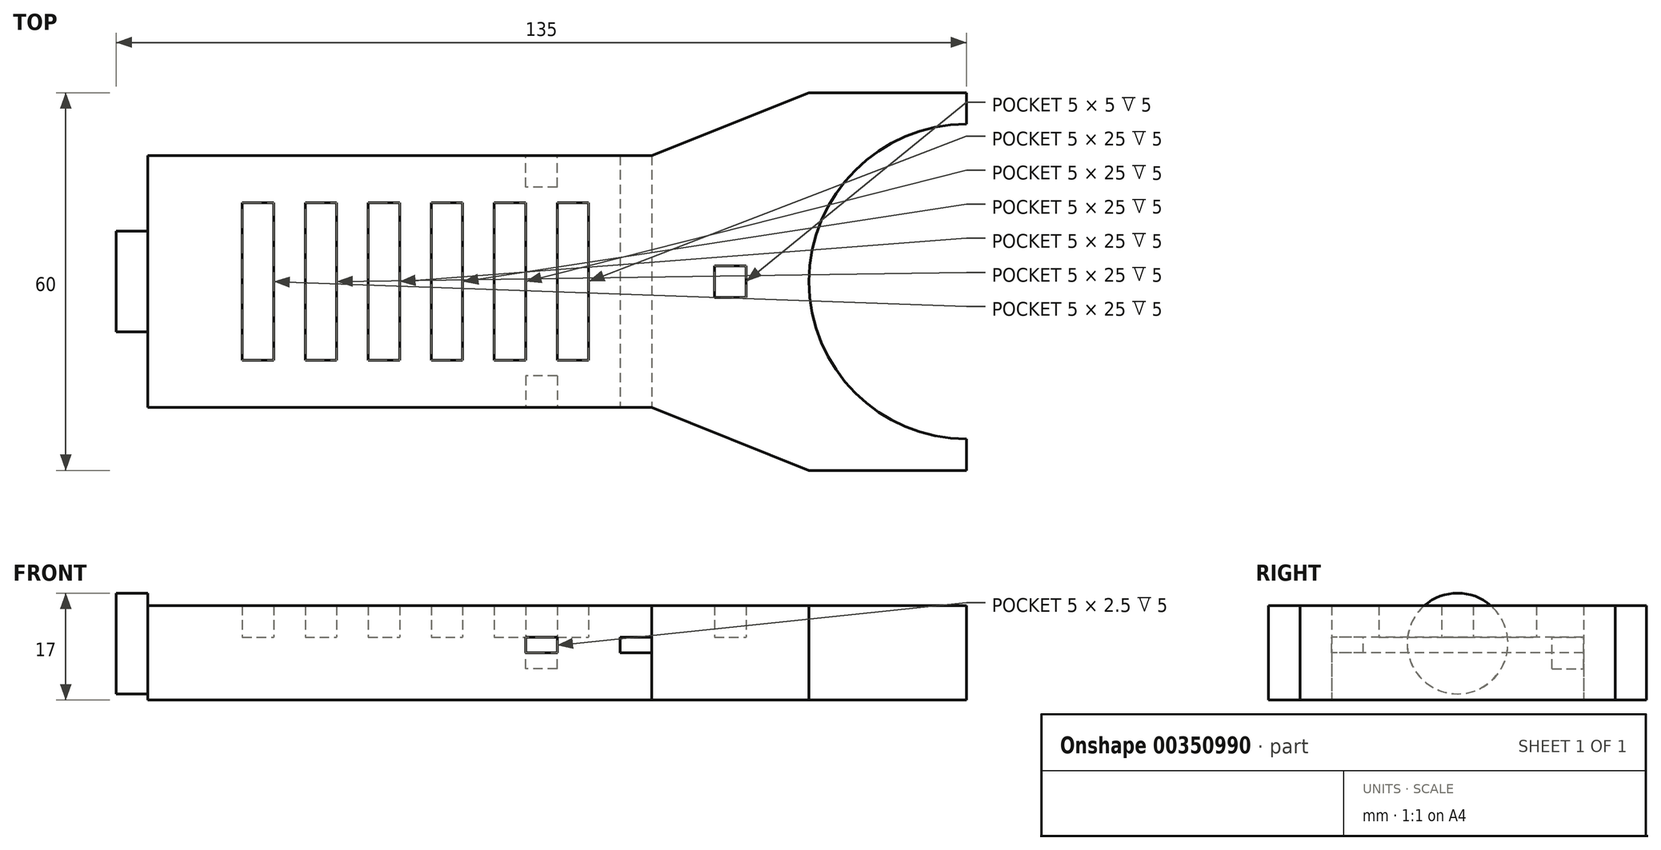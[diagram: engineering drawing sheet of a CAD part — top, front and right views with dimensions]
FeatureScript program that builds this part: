
annotation { "Feature Type Name" : "Feature", "Feature Type Description" : "" }
export const myFeature = defineFeature(function(context is Context, id is Id, definition is map)
    precondition{}
    {
        {
            var Q0;
            Q0=qCreatedBy(makeId("Top.planeOp"),FACE);
            var sketch = newSketch(context, id + "F0", { "sketchPlane" : qUnion([Q0])});
            skArc(sketch, "E0", {"start": v(46.11, 25) * mm, "mid": v(21.11, 0) * mm, "end": v(46.11, -25) * mm});
            skLineSegment(sketch, "E1", {"start": v(46.11, 25) * mm, "end": v(46.11, 30) * mm});
            skLineSegment(sketch, "E2", {"start": v(46.11, 30) * mm, "end": v(21.11, 30) * mm});
            skLineSegment(sketch, "E3", {"start": v(46.11, -25) * mm, "end": v(46.11, -30) * mm});
            skLineSegment(sketch, "E4", {"start": v(46.11, -30) * mm, "end": v(21.11, -30) * mm});
            skPoint(sketch, "E5", {"position": v(-3.89, 20) * mm});
            skPoint(sketch, "E6", {"position": v(-3.89, -20) * mm});
            skLineSegment(sketch, "E7", {"start": v(21.11, -30) * mm, "end": v(-3.89, -20) * mm});
            skLineSegment(sketch, "E8", {"start": v(21.11, 30) * mm, "end": v(-3.89, 20) * mm});
            skLineSegment(sketch, "E9", {"start": v(-3.89, 20) * mm, "end": v(-71.39, 20) * mm});
            skLineSegment(sketch, "E10", {"start": v(-71.39, -20) * mm, "end": v(-3.89, -20) * mm});
            skLineSegment(sketch, "E11", {"start": v(21.11, 0) * mm, "end": v(11.11, 0) * mm, "construction": true});
            skLineSegment(sketch, "E12", {"start": v(11.11, 0) * mm, "end": v(11.11, 2.5) * mm});
            skLineSegment(sketch, "E13", {"start": v(11.11, 2.5) * mm, "end": v(6.11, 2.5) * mm});
            skLineSegment(sketch, "E14", {"start": v(6.11, 2.5) * mm, "end": v(6.11, -2.5) * mm});
            skLineSegment(sketch, "E15", {"start": v(6.11, -2.5) * mm, "end": v(11.11, -2.5) * mm});
            skLineSegment(sketch, "E16", {"start": v(11.11, -2.5) * mm, "end": v(11.11, 0) * mm});
            skLineSegment(sketch, "E17", {"start": v(6.11, 0) * mm, "end": v(-13.89, 0) * mm, "construction": true});
            skLineSegment(sketch, "E18", {"start": v(-13.89, 0) * mm, "end": v(-13.89, 12.5) * mm});
            skLineSegment(sketch, "E19", {"start": v(-13.89, 12.5) * mm, "end": v(-18.89, 12.5) * mm});
            skLineSegment(sketch, "E20", {"start": v(-18.89, 12.5) * mm, "end": v(-18.89, -12.5) * mm});
            skLineSegment(sketch, "E21", {"start": v(-18.89, -12.5) * mm, "end": v(-13.89, -12.5) * mm});
            skLineSegment(sketch, "E22", {"start": v(-13.89, -12.5) * mm, "end": v(-13.89, 0) * mm});
            skLineSegment(sketch, "E23", {"start": v(-18.89, 0) * mm, "end": v(-23.89, 0) * mm, "construction": true});
            skLineSegment(sketch, "E24", {"start": v(-23.89, 0) * mm, "end": v(-23.89, 12.5) * mm});
            skLineSegment(sketch, "E25", {"start": v(-23.89, 12.5) * mm, "end": v(-28.89, 12.5) * mm});
            skLineSegment(sketch, "E26", {"start": v(-28.89, 12.5) * mm, "end": v(-28.89, -12.5) * mm});
            skLineSegment(sketch, "E27", {"start": v(-28.89, -12.5) * mm, "end": v(-23.89, -12.5) * mm});
            skLineSegment(sketch, "E28", {"start": v(-23.89, -12.5) * mm, "end": v(-23.89, 0) * mm});
            skLineSegment(sketch, "E29", {"start": v(-28.89, 0) * mm, "end": v(-33.89, 0) * mm, "construction": true});
            skPoint(sketch, "E29.endSnap0", {"position": v(-28.89, 0) * mm});
            skLineSegment(sketch, "E30", {"start": v(-33.89, 0) * mm, "end": v(-33.89, 12.5) * mm});
            skLineSegment(sketch, "E31", {"start": v(-33.89, 12.5) * mm, "end": v(-38.89, 12.5) * mm});
            skLineSegment(sketch, "E32", {"start": v(-38.89, 12.5) * mm, "end": v(-38.89, -12.5) * mm});
            skLineSegment(sketch, "E33", {"start": v(-38.89, -12.5) * mm, "end": v(-33.89, -12.5) * mm});
            skLineSegment(sketch, "E34", {"start": v(-33.89, -12.5) * mm, "end": v(-33.89, 0) * mm});
            skLineSegment(sketch, "E35", {"start": v(-38.89, 0) * mm, "end": v(-43.89, 0) * mm, "construction": true});
            skLineSegment(sketch, "E36", {"start": v(-43.89, 0) * mm, "end": v(-43.89, 12.5) * mm});
            skLineSegment(sketch, "E37", {"start": v(-43.89, 12.5) * mm, "end": v(-48.89, 12.5) * mm});
            skLineSegment(sketch, "E38", {"start": v(-48.89, 12.5) * mm, "end": v(-48.89, -12.5) * mm});
            skLineSegment(sketch, "E39", {"start": v(-48.89, -12.5) * mm, "end": v(-43.89, -12.5) * mm});
            skLineSegment(sketch, "E40", {"start": v(-43.89, -12.5) * mm, "end": v(-43.89, 0) * mm});
            skLineSegment(sketch, "E41", {"start": v(-48.89, 0) * mm, "end": v(-53.89, 0) * mm, "construction": true});
            skLineSegment(sketch, "E42", {"start": v(-53.89, 0) * mm, "end": v(-53.89, 12.5) * mm});
            skLineSegment(sketch, "E43", {"start": v(-53.89, 12.5) * mm, "end": v(-58.89, 12.5) * mm});
            skLineSegment(sketch, "E44", {"start": v(-58.89, 12.5) * mm, "end": v(-58.89, -12.5) * mm});
            skLineSegment(sketch, "E45", {"start": v(-58.89, -12.5) * mm, "end": v(-53.89, -12.5) * mm});
            skLineSegment(sketch, "E46", {"start": v(-53.89, -12.5) * mm, "end": v(-53.89, 0) * mm});
            skLineSegment(sketch, "E47", {"start": v(-58.89, 0) * mm, "end": v(-63.89, 0) * mm, "construction": true});
            skLineSegment(sketch, "E48", {"start": v(-63.89, 0) * mm, "end": v(-63.89, 12.5) * mm});
            skLineSegment(sketch, "E49", {"start": v(-63.89, 12.5) * mm, "end": v(-68.89, 12.5) * mm});
            skLineSegment(sketch, "E50", {"start": v(-68.89, 12.5) * mm, "end": v(-68.89, -12.5) * mm});
            skLineSegment(sketch, "E51", {"start": v(-68.89, -12.5) * mm, "end": v(-63.89, -12.5) * mm});
            skLineSegment(sketch, "E52", {"start": v(-63.89, -12.5) * mm, "end": v(-63.89, 0) * mm});
            skLineSegment(sketch, "E53", {"start": v(-71.39, -20) * mm, "end": v(-71.39, 20) * mm});
            skSolve(sketch);
        }
        {
            var Q0;
            Q0=makeQuery(id+"F0.imprint","IMPRINT",FACE,{"disambiguationData":[TD([[makeQuery(id+"F0.imprint","IMPRINT",EDGE,{"derivedFrom":sQuery(id+"F0.wireOp",EDGE,"E0")}),-1.0]])]});
            extrude(context, id + "F1", {"entities" : qUnion([Q0]), "depth" : 15 * mm});
        }
        {
            var Q0;
            Q0=makeQuery(id+"F1.opExtrude","SWEPT_FACE",FACE,{"disambiguationData":[OSD([sQuery(id+"F0.wireOp",EDGE,"E53")])]});
            extrude(context, id + "F2", {"entities" : qUnion([Q0]), "operationType" : NewBodyOperationType.ADD, "depth" : 12.5 * mm});
        }
        {
            var Q0;
            Q0=makeQuery(id+"F2.opExtrude","CAP_FACE",FACE,{"disambiguationData":[OSD([sQuery(id+"F0.wireOp",EDGE,"E53")])],"isStart":false});
            var sketch = newSketch(context, id + "F3", { "sketchPlane" : qUnion([Q0])});
            skLineSegment(sketch, "E54", {"start": v(0, 0) * mm, "end": v(0, 9) * mm, "construction": true});
            skCircle(sketch, "E55", {"center": v(0, 9) * mm, "radius": 8 * mm});
            skSolve(sketch);
        }
        {
            var Q0;
            {var subQ0=sQuery(id+"F3.wireOp",EDGE,"E55");var subQ1=sQuery(id+"F0.wireOp",EDGE,"E53");var subQ2=makeQuery(id+"F2.opExtrude","CAP_EDGE",EDGE,{"disambiguationData":[OSD([subQ1]),TDD([makeQuery(id+"F1.opExtrude","CAP_EDGE",EDGE,{"disambiguationData":[OSD([subQ1])],"isStart":false})])],"isStart":false});var subQ3=makeQuery(id+"F3.imprint","INTERSECT",VERTEX,{"disambiguationData":[OD(0.0)],"derivedFrom":[subQ2,subQ0]});Q0=makeQuery(id+"F3.imprint","IMPRINT",FACE,{"disambiguationData":[TD([[makeQuery(id+"F3.imprint","IMPRINT",EDGE,{"disambiguationData":[TD([[subQ3,1.0]])],"derivedFrom":subQ0}),1.0]])]});}
            var Q1;
            {var subQ0=sQuery(id+"F3.wireOp",EDGE,"E55");var subQ1=sQuery(id+"F0.wireOp",EDGE,"E53");var subQ2=makeQuery(id+"F2.opExtrude","CAP_EDGE",EDGE,{"disambiguationData":[OSD([subQ1]),TDD([makeQuery(id+"F1.opExtrude","CAP_EDGE",EDGE,{"disambiguationData":[OSD([subQ1])],"isStart":false})])],"isStart":false});var subQ3=makeQuery(id+"F3.imprint","INTERSECT",VERTEX,{"disambiguationData":[OD(0.0)],"derivedFrom":[subQ2,subQ0]});Q1=makeQuery(id+"F3.imprint","IMPRINT",FACE,{"disambiguationData":[TD([[makeQuery(id+"F3.imprint","IMPRINT",EDGE,{"disambiguationData":[TD([[subQ3,-1.0]])],"derivedFrom":subQ0}),1.0]])]});}
            extrude(context, id + "F4", {"entities" : qUnion([Q0, Q1]), "operationType" : NewBodyOperationType.ADD, "depth" : 5 * mm});
        }
        {
            var Q0;
            {var subQ0=sQuery(id+"F0.wireOp",EDGE,"E10");Q0=makeQuery(id+"F2.boolean.opBoolean","MERGE",FACE,{"derivedFrom":[makeQuery(id+"F1.opExtrude","SWEPT_FACE",FACE,{"disambiguationData":[OSD([subQ0])]}),makeQuery(id+"F2.opExtrude","SWEPT_FACE",FACE,{"disambiguationData":[OSD([subQ0,sQuery(id+"F0.wireOp",EDGE,"E53")])]})]});}
            var sketch = newSketch(context, id + "F5", { "sketchPlane" : qUnion([Q0])});
            skLineSegment(sketch, "E56.bottom", {"start": v(-3.89, 7.5) * mm, "end": v(-8.89, 7.5) * mm});
            skLineSegment(sketch, "E56.top", {"start": v(-3.89, 10) * mm, "end": v(-8.89, 10) * mm});
            skLineSegment(sketch, "E56.left", {"start": v(-3.89, 7.5) * mm, "end": v(-3.89, 10) * mm});
            skLineSegment(sketch, "E56.right", {"start": v(-8.89, 7.5) * mm, "end": v(-8.89, 10) * mm});
            skLineSegment(sketch, "E57.bottom", {"start": v(-8.89, 7.5) * mm, "end": v(-3.89, 7.5) * mm});
            skLineSegment(sketch, "E57.top", {"start": v(-8.89, 5) * mm, "end": v(-3.89, 5) * mm});
            skLineSegment(sketch, "E57.left", {"start": v(-8.89, 7.5) * mm, "end": v(-8.89, 5) * mm});
            skLineSegment(sketch, "E57.right", {"start": v(-3.89, 7.5) * mm, "end": v(-3.89, 5) * mm});
            skSolve(sketch);
        }
        {
            var Q0;
            Q0=makeQuery(id+"F5.imprint","IMPRINT",FACE,{"disambiguationData":[TD([[makeQuery(id+"F5.imprint","IMPRINT",EDGE,{"derivedFrom":sQuery(id+"F5.wireOp",EDGE,"E57.bottom")}),-1.0]])]});
            var Q1;
            Q1=makeQuery(id+"F5.imprint","IMPRINT",FACE,{"disambiguationData":[TD([[makeQuery(id+"F5.imprint","IMPRINT",EDGE,{"derivedFrom":sQuery(id+"F5.wireOp",EDGE,"E56.top")}),1.0]])]});
            extrude(context, id + "F6", {"entities" : qUnion([Q0, Q1]), "operationType" : NewBodyOperationType.REMOVE, "oppositeDirection" : true, "depth" : 50 * mm});
        }
        {
            var Q0;
            {var subQ0=sQuery(id+"F0.wireOp",EDGE,"E10");Q0=makeQuery(id+"F2.boolean.opBoolean","MERGE",FACE,{"derivedFrom":[makeQuery(id+"F1.opExtrude","SWEPT_FACE",FACE,{"disambiguationData":[OSD([subQ0])]}),makeQuery(id+"F2.opExtrude","SWEPT_FACE",FACE,{"disambiguationData":[OSD([subQ0,sQuery(id+"F0.wireOp",EDGE,"E53")])]})]});}
            var sketch = newSketch(context, id + "F7", { "sketchPlane" : qUnion([Q0])});
            skLineSegment(sketch, "E58", {"start": v(-8.89, 7.5) * mm, "end": v(-18.89, 7.5) * mm, "construction": true});
            skLineSegment(sketch, "E59.bottom", {"start": v(-18.89, 7.5) * mm, "end": v(-23.89, 7.5) * mm});
            skLineSegment(sketch, "E59.top", {"start": v(-18.89, 10) * mm, "end": v(-23.89, 10) * mm});
            skLineSegment(sketch, "E59.left", {"start": v(-18.89, 7.5) * mm, "end": v(-18.89, 10) * mm});
            skLineSegment(sketch, "E59.right", {"start": v(-23.89, 7.5) * mm, "end": v(-23.89, 10) * mm});
            skLineSegment(sketch, "E60.bottom", {"start": v(-23.89, 7.5) * mm, "end": v(-18.89, 7.5) * mm});
            skLineSegment(sketch, "E60.top", {"start": v(-23.89, 5) * mm, "end": v(-18.89, 5) * mm});
            skLineSegment(sketch, "E60.left", {"start": v(-23.89, 7.5) * mm, "end": v(-23.89, 5) * mm});
            skLineSegment(sketch, "E60.right", {"start": v(-18.89, 7.5) * mm, "end": v(-18.89, 5) * mm});
            skSolve(sketch);
        }
        {
            var Q0;
            Q0=makeQuery(id+"F7.imprint","IMPRINT",FACE,{"disambiguationData":[TD([[makeQuery(id+"F7.imprint","IMPRINT",EDGE,{"derivedFrom":sQuery(id+"F7.wireOp",EDGE,"E59.top")}),1.0]])]});
            var Q1;
            Q1=makeQuery(id+"F7.imprint","IMPRINT",FACE,{"disambiguationData":[TD([[makeQuery(id+"F7.imprint","IMPRINT",EDGE,{"derivedFrom":sQuery(id+"F7.wireOp",EDGE,"E60.bottom")}),-1.0]])]});
            extrude(context, id + "F8", {"entities" : qUnion([Q0, Q1]), "operationType" : NewBodyOperationType.REMOVE, "oppositeDirection" : true, "depth" : 5 * mm});
        }
        {
            var Q0;
            {var subQ0=sQuery(id+"F0.wireOp",EDGE,"E9");Q0=makeQuery(id+"F2.boolean.opBoolean","MERGE",FACE,{"derivedFrom":[makeQuery(id+"F1.opExtrude","SWEPT_FACE",FACE,{"disambiguationData":[OSD([subQ0])]}),makeQuery(id+"F2.opExtrude","SWEPT_FACE",FACE,{"disambiguationData":[OSD([subQ0,sQuery(id+"F0.wireOp",EDGE,"E53")])]})]});}
            var sketch = newSketch(context, id + "F9", { "sketchPlane" : qUnion([Q0])});
            skLineSegment(sketch, "E61", {"start": v(8.89, 7.5) * mm, "end": v(18.89, 7.5) * mm, "construction": true});
            skLineSegment(sketch, "E62.bottom", {"start": v(18.89, 7.5) * mm, "end": v(23.89, 7.5) * mm});
            skLineSegment(sketch, "E62.top", {"start": v(18.89, 10) * mm, "end": v(23.89, 10) * mm});
            skLineSegment(sketch, "E62.left", {"start": v(18.89, 7.5) * mm, "end": v(18.89, 10) * mm});
            skLineSegment(sketch, "E62.right", {"start": v(23.89, 7.5) * mm, "end": v(23.89, 10) * mm});
            skLineSegment(sketch, "E63.top", {"start": v(18.89, 5) * mm, "end": v(23.89, 5) * mm});
            skLineSegment(sketch, "E63.left", {"start": v(18.89, 7.5) * mm, "end": v(18.89, 5) * mm});
            skLineSegment(sketch, "E63.right", {"start": v(23.89, 7.5) * mm, "end": v(23.89, 5) * mm});
            skSolve(sketch);
        }
        {
            var Q0;
            Q0=makeQuery(id+"F9.imprint","IMPRINT",FACE,{"disambiguationData":[TD([[makeQuery(id+"F9.imprint","IMPRINT",EDGE,{"derivedFrom":sQuery(id+"F9.wireOp",EDGE,"E62.top")}),-1.0]])]});
            var Q1;
            Q1=makeQuery(id+"F9.imprint","IMPRINT",FACE,{"disambiguationData":[TD([[makeQuery(id+"F9.imprint","IMPRINT",EDGE,{"derivedFrom":sQuery(id+"F9.wireOp",EDGE,"E62.bottom")}),-1.0]])]});
            extrude(context, id + "F10", {"entities" : qUnion([Q0, Q1]), "operationType" : NewBodyOperationType.REMOVE, "oppositeDirection" : true, "depth" : 5 * mm});
        }
        {
            var Q0;
            Q0=makeQuery(id+"F0.imprint","IMPRINT",FACE,{"disambiguationData":[TD([[makeQuery(id+"F0.imprint","IMPRINT",EDGE,{"derivedFrom":sQuery(id+"F0.wireOp",EDGE,"E48")}),1.0]])]});
            var Q1;
            Q1=makeQuery(id+"F0.imprint","IMPRINT",FACE,{"disambiguationData":[TD([[makeQuery(id+"F0.imprint","IMPRINT",EDGE,{"derivedFrom":sQuery(id+"F0.wireOp",EDGE,"E42")}),1.0]])]});
            var Q2;
            Q2=makeQuery(id+"F0.imprint","IMPRINT",FACE,{"disambiguationData":[TD([[makeQuery(id+"F0.imprint","IMPRINT",EDGE,{"derivedFrom":sQuery(id+"F0.wireOp",EDGE,"E36")}),1.0]])]});
            var Q3;
            Q3=makeQuery(id+"F0.imprint","IMPRINT",FACE,{"disambiguationData":[TD([[makeQuery(id+"F0.imprint","IMPRINT",EDGE,{"derivedFrom":sQuery(id+"F0.wireOp",EDGE,"E30")}),1.0]])]});
            var Q4;
            Q4=makeQuery(id+"F0.imprint","IMPRINT",FACE,{"disambiguationData":[TD([[makeQuery(id+"F0.imprint","IMPRINT",EDGE,{"derivedFrom":sQuery(id+"F0.wireOp",EDGE,"E24")}),1.0]])]});
            var Q5;
            Q5=makeQuery(id+"F0.imprint","IMPRINT",FACE,{"disambiguationData":[TD([[makeQuery(id+"F0.imprint","IMPRINT",EDGE,{"derivedFrom":sQuery(id+"F0.wireOp",EDGE,"E18")}),1.0]])]});
            var Q6;
            Q6=makeQuery(id+"F0.imprint","IMPRINT",FACE,{"disambiguationData":[TD([[makeQuery(id+"F0.imprint","IMPRINT",EDGE,{"derivedFrom":sQuery(id+"F0.wireOp",EDGE,"E12")}),1.0]])]});
            extrude(context, id + "F11", {"entities" : qUnion([Q0, Q1, Q2, Q3, Q4, Q5, Q6]), "operationType" : NewBodyOperationType.ADD, "depth" : 10 * mm});
        }
    });
